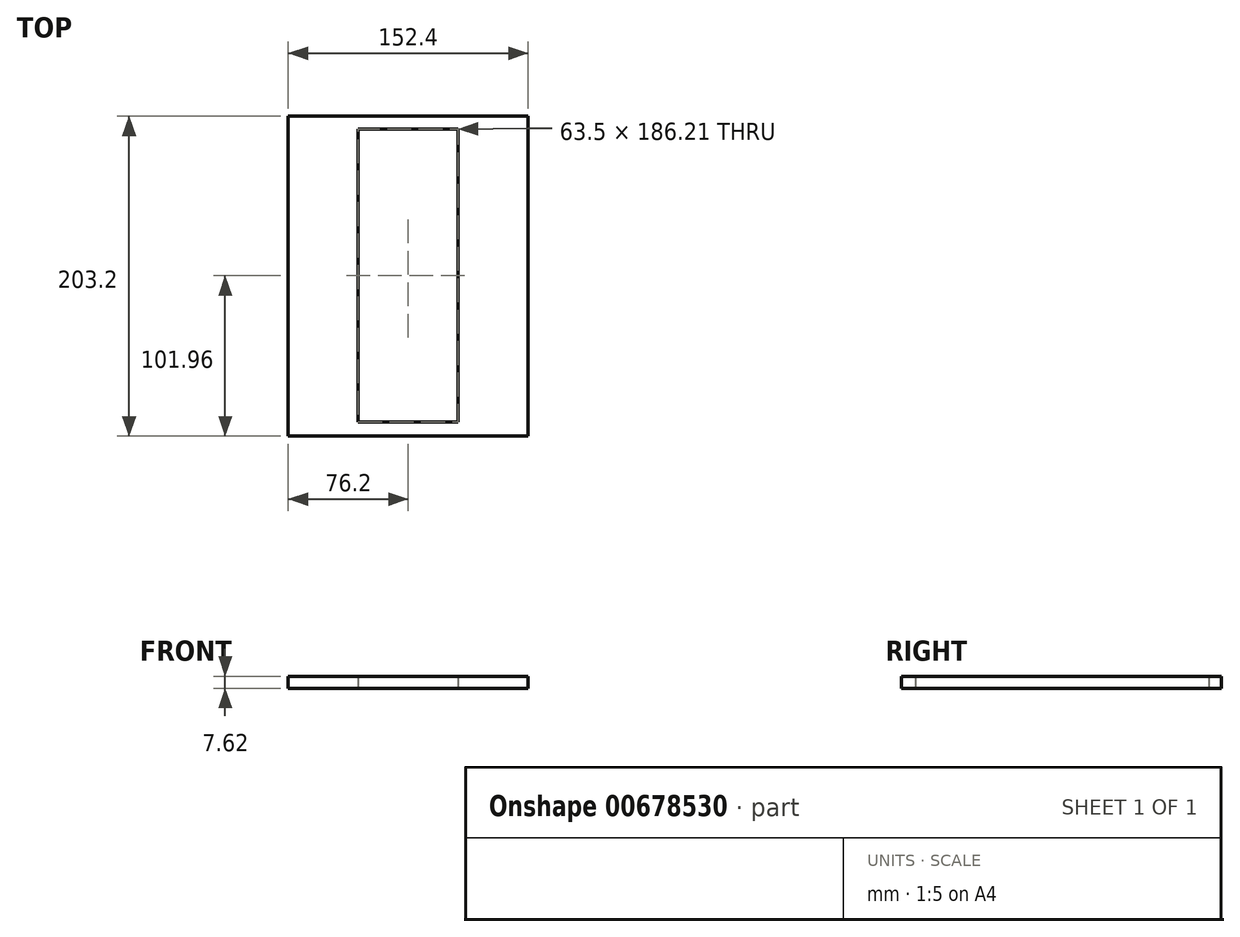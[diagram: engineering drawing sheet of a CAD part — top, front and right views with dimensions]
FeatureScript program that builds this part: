
annotation { "Feature Type Name" : "Feature", "Feature Type Description" : "" }
export const myFeature = defineFeature(function(context is Context, id is Id, definition is map)
    precondition{}
    {
        {
            var Q0;
            Q0=qCreatedBy(makeId("Top.planeOp"),FACE);
            var sketch = newSketch(context, id + "F0", { "sketchPlane" : qUnion([Q0])});
            skLineSegment(sketch, "E0.bottom", {"start": v(0, 0) * mm, "end": v(44.45, 0) * mm});
            skLineSegment(sketch, "E0.top", {"start": v(0, -203.2) * mm, "end": v(44.45, -203.2) * mm});
            skLineSegment(sketch, "E0.left", {"start": v(0, 0) * mm, "end": v(0, -203.2) * mm});
            skLineSegment(sketch, "E0.right", {"start": v(44.45, 0) * mm, "end": v(44.45, -203.2) * mm});
            skLineSegment(sketch, "E1.bottom", {"start": v(44.45, 0) * mm, "end": v(107.95, 0) * mm});
            skLineSegment(sketch, "E1.top", {"start": v(44.45, -8.14) * mm, "end": v(107.95, -8.14) * mm});
            skLineSegment(sketch, "E1.left", {"start": v(44.45, 0) * mm, "end": v(44.45, -8.14) * mm});
            skLineSegment(sketch, "E1.right", {"start": v(107.95, 0) * mm, "end": v(107.95, -8.14) * mm});
            skLineSegment(sketch, "E2.bottom", {"start": v(44.45, -203.2) * mm, "end": v(107.95, -203.2) * mm});
            skLineSegment(sketch, "E2.top", {"start": v(44.45, -194.34) * mm, "end": v(107.95, -194.34) * mm});
            skLineSegment(sketch, "E2.left", {"start": v(44.45, -203.2) * mm, "end": v(44.45, -194.34) * mm});
            skLineSegment(sketch, "E2.right", {"start": v(107.95, -203.2) * mm, "end": v(107.95, -194.34) * mm});
            skSolve(sketch);
        }
        {
            var Q0;
            Q0=makeQuery(id+"F0.imprint","IMPRINT",FACE,{"disambiguationData":[TD([[makeQuery(id+"F0.imprint","IMPRINT",EDGE,{"derivedFrom":sQuery(id+"F0.wireOp",EDGE,"E0.bottom")}),-1.0]])]});
            var Q1;
            Q1=makeQuery(id+"F0.imprint","IMPRINT",FACE,{"disambiguationData":[TD([[makeQuery(id+"F0.imprint","IMPRINT",EDGE,{"derivedFrom":sQuery(id+"F0.wireOp",EDGE,"E1.bottom")}),-1.0]])]});
            var Q2;
            Q2=makeQuery(id+"F0.imprint","IMPRINT",FACE,{"disambiguationData":[TD([[makeQuery(id+"F0.imprint","IMPRINT",EDGE,{"derivedFrom":sQuery(id+"F0.wireOp",EDGE,"E2.bottom")}),1.0]])]});
            extrude(context, id + "F1", {"entities" : qUnion([Q0, Q1, Q2]), "depth" : 7.62 * mm, "offsetDistance" : 25.4 * mm});
        }
        {
            var Q0;
            Q0=makeQuery(id+"F1.opExtrude","CAP_FACE",FACE,{"disambiguationData":[OSD([sQuery(id+"F0.wireOp",EDGE,"E0.bottom"),sQuery(id+"F0.wireOp",EDGE,"E0.top"),sQuery(id+"F0.wireOp",EDGE,"E0.left"),sQuery(id+"F0.wireOp",EDGE,"E0.right"),sQuery(id+"F0.wireOp",EDGE,"E1.bottom"),sQuery(id+"F0.wireOp",EDGE,"E1.top"),sQuery(id+"F0.wireOp",EDGE,"E1.right"),sQuery(id+"F0.wireOp",EDGE,"E2.bottom"),sQuery(id+"F0.wireOp",EDGE,"E2.top"),sQuery(id+"F0.wireOp",EDGE,"E2.right")])],"isStart":false});
            var sketch = newSketch(context, id + "F2", { "sketchPlane" : qUnion([Q0])});
            skLineSegment(sketch, "E3.bottom", {"start": v(107.95, 0) * mm, "end": v(152.4, 0) * mm});
            skLineSegment(sketch, "E3.top", {"start": v(107.95, -203.2) * mm, "end": v(152.4, -203.2) * mm});
            skLineSegment(sketch, "E3.left", {"start": v(107.95, 0) * mm, "end": v(107.95, -203.2) * mm});
            skLineSegment(sketch, "E3.right", {"start": v(152.4, 0) * mm, "end": v(152.4, -203.2) * mm});
            skSolve(sketch);
        }
        {
            var Q0;
            {var subQ1=sQuery(id+"F2.wireOp",EDGE,"E3.bottom");Q0=makeQuery(id+"F2.imprint","IMPRINT",FACE,{"disambiguationData":[TD([[makeQuery(id+"F2.imprint","IMPRINT",EDGE,{"derivedFrom":subQ1}),-1.0]])]});}
            extrude(context, id + "F3", {"entities" : qUnion([Q0]), "operationType" : NewBodyOperationType.ADD, "oppositeDirection" : true, "depth" : 7.62 * mm, "offsetDistance" : 25.4 * mm});
        }
    });
